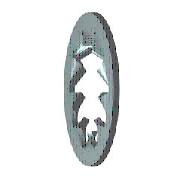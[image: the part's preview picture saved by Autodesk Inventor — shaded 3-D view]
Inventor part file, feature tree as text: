
AUTODESK INVENTOR PART (.ipt)
format: ipt  version: 2015 (Build 190159000, 159)  size: 164,864 bytes
history: native  units: mm (DEFAULTED — no unit token found)
features: sketch x2, extrude x1, pattern_circular x1, plane x1
ambient origin geometry x7: Origin, YZ Plane, XY Plane, X Axis, Y Axis, Z Axis, Center Point
bodies: Solid1 (feature_tree), Body (feature_tree)
feature tree (5):
  extrude  "Cut"  Depth=4.953mm
  pattern_circular  "Cuts"  [2 undecoded]
  plane  "Work Plane1"
  sketch  "Sketch1"  dims[d0=9.6774mm d1=4.953mm]
  sketch  "Sketch2"  dims[d2=0.6096mm d3=0.0mm d4=7.3152mm d5=1.963495mm d6=0.6096mm d7=0.0mm d8=0.14859mm d9=80.0mm d11=360.0deg d12=0.0mm d13=0.0mm d18=0.0mm d19=0.0mm]
note: 2 required parameter values undecoded (feature->parameter linkage not recoverable at this tier; creation-order binding heuristic only, values carry confidence <= 0.55)
